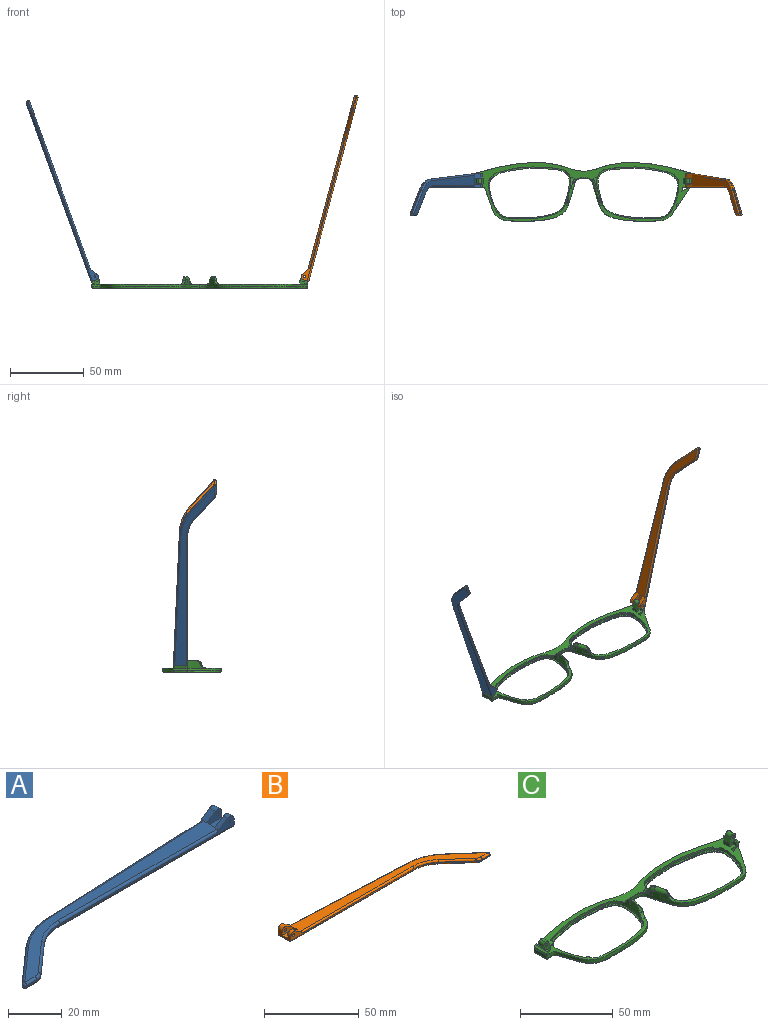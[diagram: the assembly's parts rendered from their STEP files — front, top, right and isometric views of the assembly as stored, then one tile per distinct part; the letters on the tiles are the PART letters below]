
ASSEMBLY  parts=3 mates=2
PART A: 43 faces, bbox 130.2x29.5x5.9 mm
  f0: plane 9.62x3.72mm, normal (1,0,0), area 24.7mm2, adj f1,f3,f4,f5,f10,f16,f18,f28
  f1: cylinder r=2.2mm len=3.45mm, axis (0,-1,0), area 11mm2, adj f0,f2,f4,f37
  f2: plane 6.01x3.91mm, normal (-0.55,0,0.84), area 12.7mm2, adj f1,f4,f9,f19,f37
  f3: plane 2.26x0.1mm, normal (0,0,1), area 0.1mm2, adj f0,f5,f18
  f4: plane 92.1x4.9mm, normal (0,-1,0), area 79.9mm2, adj f0,f1,f2,f14,f19,f36,f42
  f5: plane 93.42x4.13mm, normal (-0.04,1,0), area 64.8mm2, adj f0,f3,f11,f15,f17,f27,f28
  f6: plane 17.82x15.72mm, normal (-0.66,0.75,0), area 14.3mm2, adj f11,f12,f25,f30
  f7: plane 5.46x0.6mm, normal (0,-1,0), area 3.3mm2, adj f12,f13,f23,f32
  f8: plane 14.99x13.23mm, normal (0.66,-0.75,0), area 12mm2, adj f13,f14,f21,f34
  f9: plane 121.18x26.73mm, normal (0,0,1), area 627.7mm2, adj f2,f17,f19,f20,f21,f22,f23,f25
  f10: plane 129.1x27.08mm, normal (0,0,-1), area 686.5mm2, adj f0,f28,f29,f30,f32,f33,f34,f35
  f11: cylinder r=30mm len=18.52mm, axis (0,0,-1), area 12.2mm2, adj f5,f6,f26,f29
  f12: cylinder r=1mm len=1.75mm, axis (0,0,-1), area 1.5mm2, adj f6,f7,f24,f31
  f13: cylinder r=5mm len=3.31mm, axis (0,0,-1), area 2.2mm2, adj f7,f8,f22,f33
  f14: cylinder r=20mm len=13.23mm, axis (0,0,1), area 8.7mm2, adj f4,f8,f20,f35
  f15: plane 5.66x0.25mm, normal (0,0,-1), area 0.7mm2, adj f5,f17,f18
  f16: cylinder r=2.2mm len=3.45mm, axis (0,-1,0), area 14.8mm2, adj f0,f17,f18,f38
  f17: plane 6.01x3.91mm, normal (-0.55,0,0.84), area 16.9mm2, adj f5,f9,f15,f16,f18,f27,f38
  f18: plane 7.92x3.3mm, normal (0,1,0), area 15.9mm2, adj f0,f3,f15,f16,f17,f41
  f19: cylinder r=1mm len=84.18mm, axis (-1,0,0), area 131.4mm2, adj f2,f4,f9,f20
  f20: torus R=21mm, axis (0,0,1), area 23.1mm2, adj f9,f14,f19,f21
  f21: cylinder r=1mm len=15.65mm, axis (-0.75,-0.66,0), area 31.4mm2, adj f8,f9,f20,f22
  f22: torus R=4mm, axis (0,0,1), area 5.3mm2, adj f9,f13,f21,f23
  f23: cylinder r=1mm len=5.46mm, axis (-1,0,0), area 8.6mm2, adj f7,f9,f22,f24
  f24: sphere r=1mm, area 2.4mm2, adj f12,f23,f25
  f25: cylinder r=1mm len=18.48mm, axis (0.75,0.66,0), area 37.3mm2, adj f6,f9,f24,f26
  f26: torus R=29mm, axis (0,0,1), area 31.6mm2, adj f9,f11,f25,f27
  f27: cylinder r=1mm len=85.5mm, axis (1,0.04,0), area 133.5mm2, adj f5,f9,f17,f26
  f28: cylinder r=1mm len=93.46mm, axis (-1,-0.04,0), area 146.9mm2, adj f0,f5,f10,f29
  f29: torus R=29mm, axis (0,0,1), area 31.6mm2, adj f10,f11,f28,f30
  f30: cylinder r=1mm len=18.48mm, axis (-0.75,-0.66,0), area 37.3mm2, adj f6,f10,f29,f31
  f31: sphere r=1mm, area 2.4mm2, adj f12,f30,f32
  f32: cylinder r=1mm len=5.46mm, axis (1,0,0), area 8.6mm2, adj f7,f10,f31,f33
  f33: torus R=4mm, axis (0,0,1), area 5.3mm2, adj f10,f13,f32,f34
  f34: cylinder r=1mm len=15.65mm, axis (0.75,0.66,0), area 31.4mm2, adj f8,f10,f33,f35
  f35: torus R=21mm, axis (0,0,1), area 23.1mm2, adj f10,f14,f34,f36
  f36: cylinder r=1mm len=92.1mm, axis (1,0,0), area 144.7mm2, adj f0,f4,f10,f35
  f37: plane 7.92x4.7mm, normal (0,1,0), area 27mm2, adj f0,f1,f2,f39,f40,f42
  f38: plane 7.92x4.7mm, normal (0,-1,0), area 27mm2, adj f0,f16,f17,f39,f40,f41
  f39: plane 7.92x4.1mm, normal (0,0,1), area 32.5mm2, adj f0,f37,f38,f40
  f40: plane 4.1x1.4mm, normal (1,0,0), area 5.7mm2, adj f9,f37,f38,f39
  f41: cylinder r=0.5mm len=3.1mm, axis (0,-1,0), area 9.7mm2, adj f18,f38
  f42: cylinder r=0.5mm len=2.3mm, axis (0,-1,0), area 7.2mm2, adj f4,f37
PART B: 43 faces, bbox 130.2x29.5x5.9 mm
  f0: plane 9.62x3.72mm, normal (-1,0,0), area 24.7mm2, adj f1,f3,f4,f5,f10,f16,f18,f28
  f1: cylinder r=2.2mm len=3.45mm, axis (0,-1,0), area 11mm2, adj f0,f2,f4,f37
  f2: plane 6.01x3.91mm, normal (0.55,0,0.84), area 12.7mm2, adj f1,f4,f9,f19,f37
  f3: plane 2.26x0.1mm, normal (0,0,1), area 0.1mm2, adj f0,f5,f18
  f4: plane 92.1x4.9mm, normal (0,-1,0), area 78.2mm2, adj f0,f1,f2,f14,f19,f36,f42
  f5: plane 93.42x4.13mm, normal (0.04,1,0), area 64.8mm2, adj f0,f3,f11,f15,f17,f27,f28
  f6: plane 17.82x15.72mm, normal (0.66,0.75,0), area 14.3mm2, adj f11,f12,f25,f30
  f7: plane 5.46x0.6mm, normal (0,-1,0), area 3.3mm2, adj f12,f13,f23,f32
  f8: plane 14.99x13.23mm, normal (-0.66,-0.75,0), area 12mm2, adj f13,f14,f21,f34
  f9: plane 121.18x26.73mm, normal (0,0,1), area 627.7mm2, adj f2,f17,f19,f20,f21,f22,f23,f25
  f10: plane 129.1x27.08mm, normal (0,0,-1), area 686.5mm2, adj f0,f28,f29,f30,f32,f33,f34,f35
  f11: cylinder r=30mm len=18.52mm, axis (0,0,-1), area 12.2mm2, adj f5,f6,f26,f29
  f12: cylinder r=1mm len=1.75mm, axis (0,0,-1), area 1.5mm2, adj f6,f7,f24,f31
  f13: cylinder r=5mm len=3.31mm, axis (0,0,-1), area 2.2mm2, adj f7,f8,f22,f33
  f14: cylinder r=20mm len=13.23mm, axis (0,0,1), area 8.7mm2, adj f4,f8,f20,f35
  f15: plane 5.66x0.25mm, normal (0,0,-1), area 0.7mm2, adj f5,f17,f18
  f16: cylinder r=2.2mm len=3.45mm, axis (0,-1,0), area 14.8mm2, adj f0,f17,f18,f38
  f17: plane 6.01x3.91mm, normal (0.55,0,0.84), area 16.9mm2, adj f5,f9,f15,f16,f18,f27,f38
  f18: plane 7.92x3.3mm, normal (0,1,0), area 14.3mm2, adj f0,f3,f15,f16,f17,f41
  f19: cylinder r=1mm len=84.18mm, axis (1,0,0), area 131.4mm2, adj f2,f4,f9,f20
  f20: torus R=21mm, axis (0,0,1), area 23.1mm2, adj f9,f14,f19,f21
  f21: cylinder r=1mm len=15.65mm, axis (0.75,-0.66,0), area 31.4mm2, adj f8,f9,f20,f22
  f22: torus R=4mm, axis (0,0,1), area 5.3mm2, adj f9,f13,f21,f23
  f23: cylinder r=1mm len=5.46mm, axis (1,0,0), area 8.6mm2, adj f7,f9,f22,f24
  f24: sphere r=1mm, area 2.4mm2, adj f12,f23,f25
  f25: cylinder r=1mm len=18.48mm, axis (-0.75,0.66,0), area 37.3mm2, adj f6,f9,f24,f26
  f26: torus R=29mm, axis (0,0,1), area 31.6mm2, adj f9,f11,f25,f27
  f27: cylinder r=1mm len=85.5mm, axis (-1,0.04,0), area 133.5mm2, adj f5,f9,f17,f26
  f28: cylinder r=1mm len=93.46mm, axis (1,-0.04,0), area 146.9mm2, adj f0,f5,f10,f29
  f29: torus R=29mm, axis (0,0,1), area 31.6mm2, adj f10,f11,f28,f30
  f30: cylinder r=1mm len=18.48mm, axis (0.75,-0.66,0), area 37.3mm2, adj f6,f10,f29,f31
  f31: sphere r=1mm, area 2.4mm2, adj f12,f30,f32
  f32: cylinder r=1mm len=5.46mm, axis (-1,0,0), area 8.6mm2, adj f7,f10,f31,f33
  f33: torus R=4mm, axis (0,0,1), area 5.3mm2, adj f10,f13,f32,f34
  f34: cylinder r=1mm len=15.65mm, axis (-0.75,0.66,0), area 31.4mm2, adj f8,f10,f33,f35
  f35: torus R=21mm, axis (0,0,1), area 23.1mm2, adj f10,f14,f34,f36
  f36: cylinder r=1mm len=92.1mm, axis (-1,0,0), area 144.7mm2, adj f0,f4,f10,f35
  f37: plane 7.92x4.7mm, normal (0,1,0), area 25.4mm2, adj f0,f1,f2,f39,f40,f42
  f38: plane 7.92x4.7mm, normal (0,-1,0), area 25.4mm2, adj f0,f16,f17,f39,f40,f41
  f39: plane 7.92x4.1mm, normal (0,0,1), area 32.5mm2, adj f0,f37,f38,f40
  f40: plane 4.1x1.4mm, normal (-1,0,0), area 5.7mm2, adj f9,f37,f38,f39
  f41: cylinder r=0.88mm len=3.1mm, axis (0,-1,0), area 17mm2, adj f18,f38
  f42: cylinder r=0.88mm len=2.3mm, axis (0,-1,0), area 12.6mm2, adj f4,f37
PART C: 118 faces, bbox 148.1x40.9x17.9 mm
  f0: bspline ~1.82x1.22mm, area 0.7mm2, adj f2,f7,f37,f52
  f1: plane 147.66x40.42mm, normal (0,0,1), area 851.9mm2, adj f4,f5,f6,f7,f8,f12,f20,f23
  f2: bspline ~6.1x4.93mm, area 12.7mm2, adj f0,f7,f37,f41,f43,f52,f53
  f3: plane 4.46x1.45mm, normal (0,0,1), area 0.1mm2, adj f7,f38
  f4: plane 1.23x0.04mm, normal (0,0,1), area 0mm2, adj f1,f7,f22
  f5: plane 6.97x5.07mm, normal (0,1,0), area 22.7mm2, adj f1,f20,f21,f25,f27,f28,f30,f31
  f6: plane 3.2x2.36mm, normal (0,-1,0), area 5.7mm2, adj f1,f20,f26,f29
  f7: extruded ~73.26x39.84mm, area 291.2mm2, adj f0,f1,f2,f3,f4,f8,f13,f14
  f8: extruded ~35.39x5.69mm, area 72.2mm2, adj f1,f7,f18,f67
  f9: plane 144.78x37.85mm, normal (0,0,-1), area 582.4mm2, adj f13,f15,f17,f18,f19,f71,f73,f75
  f10: plane 56.08x35.45mm, normal (0,0,1), area 128.4mm2, adj f11,f19
  f11: extruded ~55.7x35.36mm, area 159.9mm2, adj f10,f12
  f12: extruded ~55.7x35.36mm, area 219.1mm2, adj f1,f11,f39,f40,f41,f42,f43,f44
  f13: bspline ~73.27x30.39mm, area 161.7mm2, adj f7,f9,f14,f71
  f14: bspline ~1x1mm, area 0.8mm2, adj f7,f13,f15
  f15: bspline ~8.99x1.23mm, area 12.6mm2, adj f7,f9,f14,f16
  f16: bspline ~1.04x1mm, area 0.7mm2, adj f7,f15,f17
  f17: bspline ~45.86x8.59mm, area 59.8mm2, adj f7,f9,f16,f18
  f18: bspline ~37.01x6.7mm, area 56.6mm2, adj f8,f9,f17,f76
  f19: bspline ~56.23x35.9mm, area 235.3mm2, adj f9,f10
  f20: plane 4x2.36mm, normal (-1,0,0), area 9.5mm2, adj f1,f5,f6,f21
  f21: plane 4x0.02mm, normal (0.34,0,0.94), area 0.1mm2, adj f5,f20,f28
  f22: plane 2.76x2.53mm, normal (0,-1,0), area 3.9mm2, adj f4,f26,f27,f35,f56
  f23: plane 7.67x1.6mm, normal (0.94,0,-0.34), area 13mm2, adj f1,f35,f36,f56
  f24: plane 2.1x1.69mm, normal (0,1,0), area 2.8mm2, adj f1,f25,f27,f36,f56
  f25: plane 3.3x2.1mm, normal (-1,0,0), area 6.9mm2, adj f1,f5,f24,f27
  f26: plane 2.35x2.1mm, normal (-1,0,0), area 4.9mm2, adj f1,f6,f22,f27,f29
  f27: plane 9.65x1.24mm, normal (0,0,1), area 8.2mm2, adj f5,f22,f24,f25,f26,f29,f30,f56
  f28: plane 4x3.31mm, normal (-0.94,0,0.34), area 14.1mm2, adj f5,f21,f29,f32
  f29: plane 5.77x5.06mm, normal (0,-1,0), area 17mm2, adj f6,f26,f27,f28,f30,f31,f32,f33
  f30: plane 4x2.21mm, normal (0.94,0,-0.34), area 9.4mm2, adj f5,f27,f29,f33
  f31: plane 4x0.01mm, normal (0.34,0,0.94), area 0mm2, adj f5,f29,f32,f33
  f32: cylinder r=1.98mm len=4mm, axis (0,1,0), area 12.4mm2, adj f5,f28,f29,f31
  f33: cylinder r=1.98mm len=4mm, axis (0,-1,0), area 12.4mm2, adj f5,f29,f30,f31
  f34: cylinder r=0.88mm len=4mm, axis (0,-1,0), area 22mm2, adj f5,f29
  f35: cone r=1mm half-angle=20deg, axis (0,0,1), area 2.3mm2, adj f1,f22,f23,f56
  f36: cylinder r=1mm len=2.28mm, axis (-0.34,0,-0.94), area 3mm2, adj f1,f23,f24,f56
  f37: extruded ~3.67x3.11mm, area 5.9mm2, adj f0,f2,f7,f59
  f38: extruded ~4.44x3.32mm, area 15.1mm2, adj f3,f7,f42,f43,f55
  f39: extruded ~4.98x1.36mm, area 6.6mm2, adj f12,f41
  f40: plane 3.63x0.97mm, normal (0,0,1), area 0.3mm2, adj f12,f41,f43
  f41: bspline ~15.5x15.35mm, area 6.4mm2, adj f2,f12,f39,f40,f54
  f42: bspline ~7.26x7.26mm, area 6.3mm2, adj f12,f38,f43,f55
  f43: bspline ~10.29x4.84mm, area 21.4mm2, adj f2,f7,f12,f38,f40,f42
  f44: plane 3.14x2.69mm, normal (0,0,-1), area 3.8mm2, adj f12,f45
  f45: cylinder r=2.28mm len=3.13mm, axis (0,0,1), area 2.4mm2, adj f1,f12,f44
  f46: cylinder r=1.3mm len=0.57mm, axis (0,0,1), area 0.4mm2, adj f1,f12,f47
  f47: plane 0.57x0.44mm, normal (0,0,-1), area 0mm2, adj f12,f46
  f48: cylinder r=1.3mm len=1.49mm, axis (0,0,1), area 1mm2, adj f1,f7,f49
  f49: plane 1.51x1.13mm, normal (0,0,-1), area 0.5mm2, adj f7,f48
  f50: plane 1.95x1.68mm, normal (0,0,-1), area 1.5mm2, adj f12,f51
  f51: cylinder r=1.3mm len=1.93mm, axis (0,0,1), area 1.5mm2, adj f1,f12,f50
  f52: bspline ~2.66x2.04mm, area 1.9mm2, adj f0,f2,f7,f53,f58
  f53: bspline ~3.55x3.47mm, area 3.7mm2, adj f1,f2,f52,f54,f58
  f54: bspline ~4.65x3.9mm, area 7.6mm2, adj f1,f12,f41,f53
  f55: bspline ~3.7x3.66mm, area 7.8mm2, adj f1,f7,f12,f38,f42
  f56: plane 9.71x1.44mm, normal (0.34,0,0.94), area 13.9mm2, adj f22,f23,f24,f27,f35,f36
  f57: bspline ~6.38x2.14mm, area 2.6mm2, adj f1,f7,f58,f115
  f58: bspline ~2.1x1.46mm, area 0.6mm2, adj f7,f52,f53,f57
  f59: bspline ~5.24x1.75mm, area 0mm2, adj f7,f37
  f60: bspline ~2.19x1.4mm, area 0.7mm2, adj f61,f66,f95,f110
  f61: bspline ~6.1x4.93mm, area 12.6mm2, adj f60,f66,f95,f99,f101,f110,f111
  f62: plane 4.46x1.45mm, normal (0,0,1), area 0.1mm2, adj f66,f96
  f63: plane 1.23x0.04mm, normal (0,0,1), area 0mm2, adj f1,f66,f80
  f64: plane 6.97x5.07mm, normal (0,1,0), area 22.7mm2, adj f1,f78,f79,f83,f85,f86,f88,f89
  f65: plane 3.2x2.36mm, normal (0,-1,0), area 5.7mm2, adj f1,f78,f84,f87
  f66: extruded ~73.26x39.84mm, area 291.2mm2, adj f1,f7,f60,f61,f62,f63,f67,f71
  f67: extruded ~35.39x5.69mm, area 72.2mm2, adj f1,f8,f66,f76
  f68: plane 56.08x35.45mm, normal (0,0,1), area 128.4mm2, adj f69,f77
  f69: extruded ~55.7x35.36mm, area 159.9mm2, adj f68,f70
  f70: extruded ~55.7x35.36mm, area 219.1mm2, adj f1,f69,f97,f98,f99,f100,f101,f102
  f71: bspline ~73.83x30.39mm, area 161.7mm2, adj f9,f13,f66,f72
  f72: bspline ~1x1mm, area 0.8mm2, adj f66,f71,f73
  f73: bspline ~8.99x1.23mm, area 12.6mm2, adj f9,f66,f72,f74
  f74: bspline ~1.04x1mm, area 0.8mm2, adj f66,f73,f75
  f75: bspline ~45.86x8.59mm, area 59.8mm2, adj f9,f66,f74,f76
  f76: bspline ~37.01x6.7mm, area 56.6mm2, adj f9,f18,f67,f75
  f77: bspline ~56.22x35.9mm, area 235.3mm2, adj f9,f68
  f78: plane 4x2.36mm, normal (1,0,0), area 9.5mm2, adj f1,f64,f65,f79
  f79: plane 4x0.02mm, normal (-0.34,0,0.94), area 0.1mm2, adj f64,f78,f86
  f80: plane 2.76x2.53mm, normal (0,-1,0), area 3.9mm2, adj f63,f84,f85,f93,f114
  f81: plane 7.67x1.6mm, normal (-0.94,0,-0.34), area 13mm2, adj f1,f93,f94,f114
  f82: plane 2.1x1.69mm, normal (0,1,0), area 2.8mm2, adj f1,f83,f85,f94,f114
  f83: plane 3.3x2.1mm, normal (1,0,0), area 6.9mm2, adj f1,f64,f82,f85
  f84: plane 2.35x2.1mm, normal (1,0,0), area 4.9mm2, adj f1,f65,f80,f85,f87
  f85: plane 9.65x1.24mm, normal (0,0,1), area 8.2mm2, adj f64,f80,f82,f83,f84,f87,f88,f114
  f86: plane 4x3.31mm, normal (0.94,0,0.34), area 14.1mm2, adj f64,f79,f87,f90
  f87: plane 5.77x5.06mm, normal (0,-1,0), area 17mm2, adj f65,f84,f85,f86,f88,f89,f90,f91
  f88: plane 4x2.21mm, normal (-0.94,0,-0.34), area 9.4mm2, adj f64,f85,f87,f91
  f89: plane 4x0.01mm, normal (-0.34,0,0.94), area 0mm2, adj f64,f87,f90,f91
  f90: cylinder r=1.98mm len=4mm, axis (0,1,0), area 12.4mm2, adj f64,f86,f87,f89
  f91: cylinder r=1.98mm len=4mm, axis (0,-1,0), area 12.4mm2, adj f64,f87,f88,f89
  f92: cylinder r=0.88mm len=4mm, axis (0,-1,0), area 22mm2, adj f64,f87
  f93: cone r=1mm half-angle=20deg, axis (0,0,1), area 2.3mm2, adj f1,f80,f81,f114
  f94: cylinder r=1mm len=2.28mm, axis (0.34,0,-0.94), area 3mm2, adj f1,f81,f82,f114
  f95: extruded ~3.67x3.11mm, area 5.9mm2, adj f60,f61,f66,f117
  f96: extruded ~4.44x3.32mm, area 15.1mm2, adj f62,f66,f100,f101,f113
  f97: extruded ~4.98x1.36mm, area 6.6mm2, adj f70,f99
  f98: plane 3.63x0.97mm, normal (0,0,1), area 0.3mm2, adj f70,f99,f101
  f99: bspline ~15.5x15.35mm, area 6.4mm2, adj f61,f70,f97,f98,f112
  f100: bspline ~7.26x7.26mm, area 6.2mm2, adj f70,f96,f101,f113
  f101: bspline ~10.29x4.84mm, area 21.5mm2, adj f61,f66,f70,f96,f98,f100
  f102: plane 3.14x2.69mm, normal (0,0,-1), area 3.8mm2, adj f70,f103
  f103: cylinder r=2.28mm len=3.13mm, axis (0,0,1), area 2.4mm2, adj f1,f70,f102
  f104: cylinder r=1.3mm len=0.57mm, axis (0,0,1), area 0.4mm2, adj f1,f70,f105
  f105: plane 0.57x0.44mm, normal (0,0,-1), area 0mm2, adj f70,f104
  f106: cylinder r=1.3mm len=1.49mm, axis (0,0,1), area 1mm2, adj f1,f66,f107
  f107: plane 1.51x1.13mm, normal (0,0,-1), area 0.5mm2, adj f66,f106
  f108: plane 1.95x1.68mm, normal (0,0,-1), area 1.5mm2, adj f70,f109
  f109: cylinder r=1.3mm len=1.93mm, axis (0,0,1), area 1.5mm2, adj f1,f70,f108
  f110: bspline ~2.65x2.03mm, area 1.9mm2, adj f60,f61,f66,f111,f116
  f111: bspline ~3.55x3.47mm, area 3.7mm2, adj f1,f61,f110,f112,f116
  f112: bspline ~4.51x3.85mm, area 7.6mm2, adj f1,f70,f99,f111
  f113: bspline ~3.7x3.66mm, area 7.8mm2, adj f1,f66,f70,f96,f100
  f114: plane 9.71x1.44mm, normal (-0.34,0,0.94), area 13.9mm2, adj f80,f81,f82,f85,f93,f94
  f115: bspline ~6.38x2.14mm, area 2.6mm2, adj f1,f57,f66,f116
  f116: bspline ~2.1x1.46mm, area 0.6mm2, adj f66,f110,f111,f115
  f117: bspline ~5.24x1.75mm, area 0mm2, adj f66,f95
PLACE A rot(axis=(0,1,0),70deg) t=(-84.77,-5.75,56)mm
PLACE B rot(axis=(0,-1,0),75deg) t=(68.2,-5.75,-61.61)mm
PLACE C t=(10.15,-1.13,-5.77)mm
MATE revolute A.f1 <-> C.f90  axis (0,-1,0) through (-60.89,2.72,1.22)mm
MATE revolute B.f41 <-> C.f33  axis (0,-1,0) through (81.2,2.72,1.21)mm
